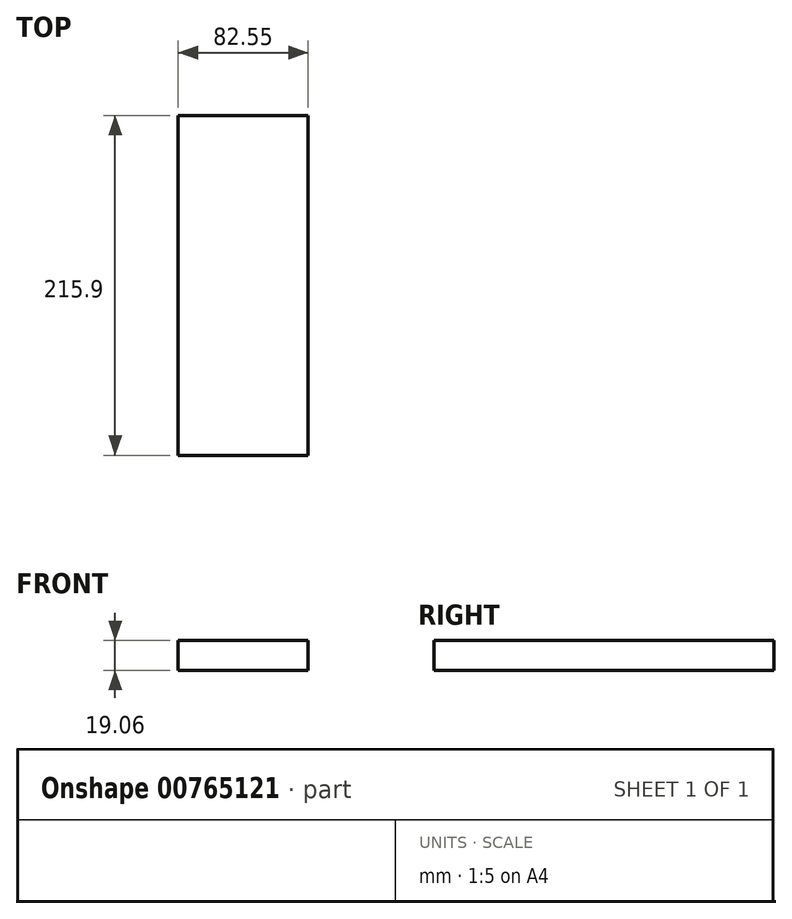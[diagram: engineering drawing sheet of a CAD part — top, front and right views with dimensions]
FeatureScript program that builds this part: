
annotation { "Feature Type Name" : "Feature", "Feature Type Description" : "" }
export const myFeature = defineFeature(function(context is Context, id is Id, definition is map)
    precondition{}
    {
        {
            var Q0;
            Q0=qCreatedBy(makeId("Front.planeOp"),FACE);
            var sketch = newSketch(context, id + "F0", { "sketchPlane" : qUnion([Q0])});
            skLineSegment(sketch, "E0.bottom", {"start": v(41.28, -9.52) * mm, "end": v(-41.28, -9.53) * mm});
            skLineSegment(sketch, "E0.top", {"start": v(41.28, 9.53) * mm, "end": v(-41.28, 9.53) * mm});
            skLineSegment(sketch, "E0.left", {"start": v(41.28, -9.52) * mm, "end": v(41.28, 9.53) * mm});
            skLineSegment(sketch, "E0.right", {"start": v(-41.28, -9.53) * mm, "end": v(-41.28, 9.53) * mm});
            skPoint(sketch, "E0.middle", {"position": v(0, 0) * mm});
            skLineSegment(sketch, "E1.bottom", {"start": v(111.12, 38.1) * mm, "end": v(60.32, 38.1) * mm});
            skLineSegment(sketch, "E1.top", {"start": v(111.12, 66.68) * mm, "end": v(60.32, 66.68) * mm});
            skLineSegment(sketch, "E1.left", {"start": v(111.12, 38.1) * mm, "end": v(111.12, 66.68) * mm});
            skLineSegment(sketch, "E1.right", {"start": v(60.32, 38.1) * mm, "end": v(60.32, 66.68) * mm});
            skPoint(sketch, "E1.middle", {"position": v(85.72, 52.39) * mm});
            skLineSegment(sketch, "E2", {"start": v(41.28, 9.53) * mm, "end": v(41.28, 27) * mm});
            skArc(sketch, "E3", {"start": v(41.27, 27) * mm, "mid": v(45.92, 38.23) * mm, "end": v(57.15, 42.88) * mm});
            skLineSegment(sketch, "E4", {"start": v(57.15, 42.88) * mm, "end": v(78.93, 42.88) * mm});
            skLineSegment(sketch, "E5.0", {"start": v(57.15, 61.93) * mm, "end": v(78.93, 61.93) * mm});
            skArc(sketch, "E5.1", {"start": v(22.23, 27) * mm, "mid": v(32.45, 51.7) * mm, "end": v(57.15, 61.93) * mm});
            skLineSegment(sketch, "E5.2", {"start": v(22.22, 9.53) * mm, "end": v(22.22, 27) * mm});
            skFitSpline(sketch, "E6", {"points": [v(-41.28, 9.52) * mm, v(57.15, 61.93) * mm], "startDerivative": vector(3.1, 74) * mm, "endDerivative": vector(118.97, 5.6) * mm});
            skSolve(sketch);
        }
        {
            var Q0;
            Q0=makeQuery(id+"F0.imprint","IMPRINT",FACE,{"disambiguationData":[TD([[makeQuery(id+"F0.imprint","IMPRINT",EDGE,{"derivedFrom":sQuery(id+"F0.wireOp",EDGE,"E0.bottom")}),-1.0]])]});
            extrude(context, id + "F1", {"entities" : qUnion([Q0]), "endBound" : BoundingType.SYMMETRIC, "depth" : 127 * mm, "offsetDistance" : 25.4 * mm});
        }
        {
            var Q0;
            Q0=makeQuery(id+"F1.opExtrude","CAP_FACE",FACE,{"disambiguationData":[OSD([sQuery(id+"F0.wireOp",EDGE,"E0.bottom"),sQuery(id+"F0.wireOp",EDGE,"E0.top"),sQuery(id+"F0.wireOp",EDGE,"E0.left"),sQuery(id+"F0.wireOp",EDGE,"E0.right")])],"isStart":false});
            extrude(context, id + "F2", {"entities" : qUnion([Q0]), "operationType" : NewBodyOperationType.ADD, "depth" : 25.4 * mm, "offsetDistance" : 25.4 * mm});
        }
        {
            var Q0;
            Q0=makeQuery(id+"F2.opExtrude","CAP_FACE",FACE,{"disambiguationData":[OSD([sQuery(id+"F0.wireOp",EDGE,"E0.bottom"),sQuery(id+"F0.wireOp",EDGE,"E0.top"),sQuery(id+"F0.wireOp",EDGE,"E0.left"),sQuery(id+"F0.wireOp",EDGE,"E0.right")])],"isStart":false});
            extrude(context, id + "F3", {"entities" : qUnion([Q0]), "operationType" : NewBodyOperationType.ADD, "endBound" : BoundingType.SYMMETRIC, "depth" : 127 * mm, "offsetDistance" : 25.4 * mm});
        }
    });
